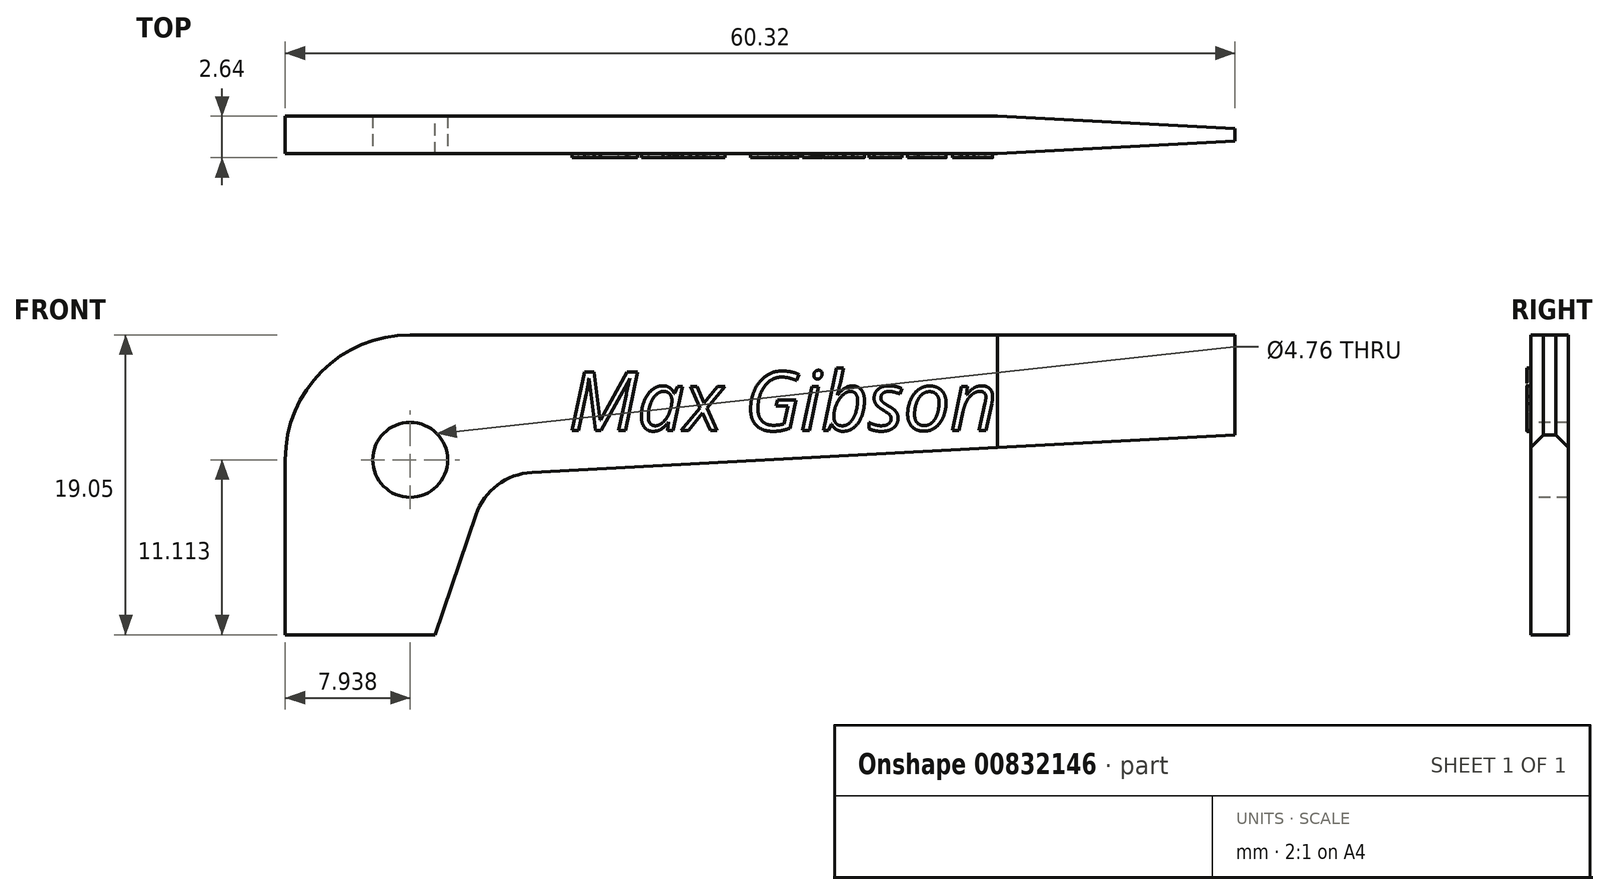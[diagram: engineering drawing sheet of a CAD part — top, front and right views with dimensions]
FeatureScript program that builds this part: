
annotation { "Feature Type Name" : "Feature", "Feature Type Description" : "" }
export const myFeature = defineFeature(function(context is Context, id is Id, definition is map)
    precondition{}
    {
        {
            var Q0;
            Q0=qCreatedBy(makeId("Front.planeOp"),FACE);
            var sketch = newSketch(context, id + "F0", { "sketchPlane" : qUnion([Q0])});
            skLineSegment(sketch, "E0.top", {"start": v(7.94, 19.05) * mm, "end": v(60.33, 19.05) * mm});
            skLineSegment(sketch, "E0.left", {"start": v(0, 0) * mm, "end": v(0, 11.11) * mm});
            skLineSegment(sketch, "E1", {"start": v(9.53, 0) * mm, "end": v(12.12, 7.63) * mm});
            skLineSegment(sketch, "E2", {"start": v(60.33, 12.7) * mm, "end": v(15.66, 10.31) * mm});
            skLineSegment(sketch, "E3", {"start": v(60.33, 19.05) * mm, "end": v(60.33, 12.7) * mm});
            skArc(sketch, "E4", {"start": v(15.66, 10.31) * mm, "mid": v(13.48, 9.51) * mm, "end": v(12.12, 7.63) * mm});
            skPoint(sketch, "E5.visualSharp", {"position": v(0, 19.05) * mm});
            skArc(sketch, "E5.filletArc", {"start": v(7.94, 19.05) * mm, "mid": v(2.32, 16.73) * mm, "end": v(0, 11.11) * mm});
            skLineSegment(sketch, "E6", {"start": v(9.53, 0) * mm, "end": v(0, 0) * mm});
            skSolve(sketch);
        }
        {
            var Q0;
            Q0 = qSketchRegion(id + "F0", true);
            extrude(context, id + "F1", {"entities" : qUnion([Q0]), "depth" : 2.38 * mm, "offsetDistance" : 25.4 * mm});
        }
        {
            var Q0;
            Q0=makeQuery(id+"F1.opExtrude","CAP_FACE",FACE,{"disambiguationData":[OSD([sQuery(id+"F0.wireOp",EDGE,"E0.top"),sQuery(id+"F0.wireOp",EDGE,"E0.left"),sQuery(id+"F0.wireOp",EDGE,"E1"),sQuery(id+"F0.wireOp",EDGE,"E2"),sQuery(id+"F0.wireOp",EDGE,"E3"),sQuery(id+"F0.wireOp",EDGE,"E4"),sQuery(id+"F0.wireOp",EDGE,"E5.filletArc"),sQuery(id+"F0.wireOp",EDGE,"E6")])],"isStart":false});
            var sketch = newSketch(context, id + "F2", { "sketchPlane" : qUnion([Q0])});
            skCircle(sketch, "E7", {"center": v(7.94, 11.11) * mm, "radius": 2.38 * mm});
            skSolve(sketch);
        }
        {
            var Q0;
            Q0=makeQuery(id+"F2.imprint","IMPRINT",FACE,{"disambiguationData":[TD([[makeQuery(id+"F2.imprint","IMPRINT",EDGE,{"derivedFrom":sQuery(id+"F2.wireOp",EDGE,"E7")}),1.0]])]});
            extrude(context, id + "F3", {"entities" : qUnion([Q0]), "operationType" : NewBodyOperationType.REMOVE, "oppositeDirection" : true, "depth" : 25.4 * mm, "offsetDistance" : 25.4 * mm});
        }
        {
            var Q0;
            Q0=makeQuery(id+"F1.opExtrude","SWEPT_FACE",FACE,{"disambiguationData":[OSD([sQuery(id+"F0.wireOp",EDGE,"E0.top")])]});
            var sketch = newSketch(context, id + "F4", { "sketchPlane" : qUnion([Q0])});
            skLineSegment(sketch, "E8", {"start": v(45.24, 0) * mm, "end": v(60.33, -0.8) * mm});
            skLineSegment(sketch, "E9", {"start": v(60.33, -0.8) * mm, "end": v(60.33, 0) * mm});
            skLineSegment(sketch, "E10", {"start": v(60.33, 0) * mm, "end": v(45.24, 0) * mm});
            skLineSegment(sketch, "E11.MirrorCS", {"start": v(45.24, -2.38) * mm, "end": v(60.33, -1.59) * mm});
            skLineSegment(sketch, "E12.MirrorCS", {"start": v(60.33, -2.38) * mm, "end": v(45.24, -2.38) * mm});
            skLineSegment(sketch, "E13.MirrorCS", {"start": v(60.33, -1.59) * mm, "end": v(60.33, -2.38) * mm});
            skSolve(sketch);
        }
        {
            var Q0;
            Q0=makeQuery(id+"F4.imprint","IMPRINT",FACE,{"disambiguationData":[TD([[makeQuery(id+"F4.imprint","IMPRINT",EDGE,{"derivedFrom":sQuery(id+"F4.wireOp",EDGE,"E11.MirrorCS")}),-1.0]])]});
            var Q1;
            Q1=makeQuery(id+"F4.imprint","IMPRINT",FACE,{"disambiguationData":[TD([[makeQuery(id+"F4.imprint","IMPRINT",EDGE,{"derivedFrom":sQuery(id+"F4.wireOp",EDGE,"E8")}),1.0]])]});
            extrude(context, id + "F5", {"entities" : qUnion([Q0, Q1]), "operationType" : NewBodyOperationType.REMOVE, "oppositeDirection" : true, "depth" : 25.4 * mm, "offsetDistance" : 25.4 * mm});
        }
        {
            var Q0;
            Q0=makeQuery(id+"F1.opExtrude","CAP_FACE",FACE,{"disambiguationData":[OSD([sQuery(id+"F0.wireOp",EDGE,"E0.top"),sQuery(id+"F0.wireOp",EDGE,"E0.left"),sQuery(id+"F0.wireOp",EDGE,"E1"),sQuery(id+"F0.wireOp",EDGE,"E2"),sQuery(id+"F0.wireOp",EDGE,"E3"),sQuery(id+"F0.wireOp",EDGE,"E4"),sQuery(id+"F0.wireOp",EDGE,"E5.filletArc"),sQuery(id+"F0.wireOp",EDGE,"E6")])],"isStart":false});
            var sketch = newSketch(context, id + "F6", { "sketchPlane" : qUnion([Q0])});
            skText(sketch, "E14", { "text": "Max Gibson", "fontName": "OpenSans-Italic.ttf"});
            const initialGuessF6  = {"E14": [0.018, 0.01297, 1, 0, 0.00376]};
            skSetInitialGuess(sketch, initialGuessF6);
            skSolve(sketch);
        }
        {
            var Q0;
            Q0 = qSketchRegion(id + "F6", true);
            extrude(context, id + "F7", {"entities" : qUnion([Q0]), "operationType" : NewBodyOperationType.ADD, "depth" : 0.25 * mm, "offsetDistance" : 25.4 * mm});
        }
    });
